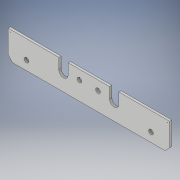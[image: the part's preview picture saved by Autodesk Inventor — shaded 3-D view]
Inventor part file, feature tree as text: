
AUTODESK INVENTOR PART (.ipt)
format: ipt  version: 2017 (Build 210142000, 142)  size: 167,424 bytes
history: native  units: in
note: dims shown in document units (in); Inventor stores cm internally (conversion verified against a paired STEP export)
features: extrude x7, sketch x7, chamfer x2
ambient origin geometry x8: Origin, YZ Plane, XZ Plane, XY Plane, X Axis, Y Axis, Z Axis, Center Point
bodies: Solid1 (feature_tree)
feature tree (16):
  extrude  "Extrusion1"  Depth=3.0in
  chamfer  "Chamfer1"  Distance=0.25in
  chamfer  "Chamfer2"  Distance=0.5in Angle=45.0deg
  extrude  "Extrusion2"  Depth=0.5in
  extrude  "Extrusion3"  Depth=1.0in
  extrude  "Extrusion4"  Depth=1.0in TaperAngle=0.0deg
  extrude  "Extrusion5"  Depth=1.0in
  extrude  "Extrusion6"  Depth=1.0in
  extrude  "Extrusion7"  Depth=0.5in
  sketch  "Sketch1"  dims[d0=17.5in d1=3.0in d2=0.25in d3=0.0in d4=0.5in d5=0.125in d6=45.0deg]
  sketch  "Sketch2"  dims[d7=0.5in d8=0.125in d9=45.0deg d10=6.0in]
  sketch  "Sketch3"  dims[d11=1.0in d12=1.0in]
  sketch  "Sketch4"  dims[d13=1.0in d14=0.0in d15=1.0in d16=0.0in]
  sketch  "Sketch5"  dims[d17=1.0in d18=0.0in d19=2.0in]
  sketch  "Sketch6"  dims[d20=1.0in d21=1.0in]
  sketch  "Sketch7"  dims[d22=2.0in d23=0.5in d24=0.5in d25=1.0in d26=0.0in d27=0.25in d28=0.25in d29=0.25in d30=0.25in d31=0.05in d32=0.05in d33=1.0in d34=0.0in d35=1.0in d36=1.25in d37=1.0in d38=1.25in d39=0.5in d40=0.5in d41=1.0in d42=0.0in]
